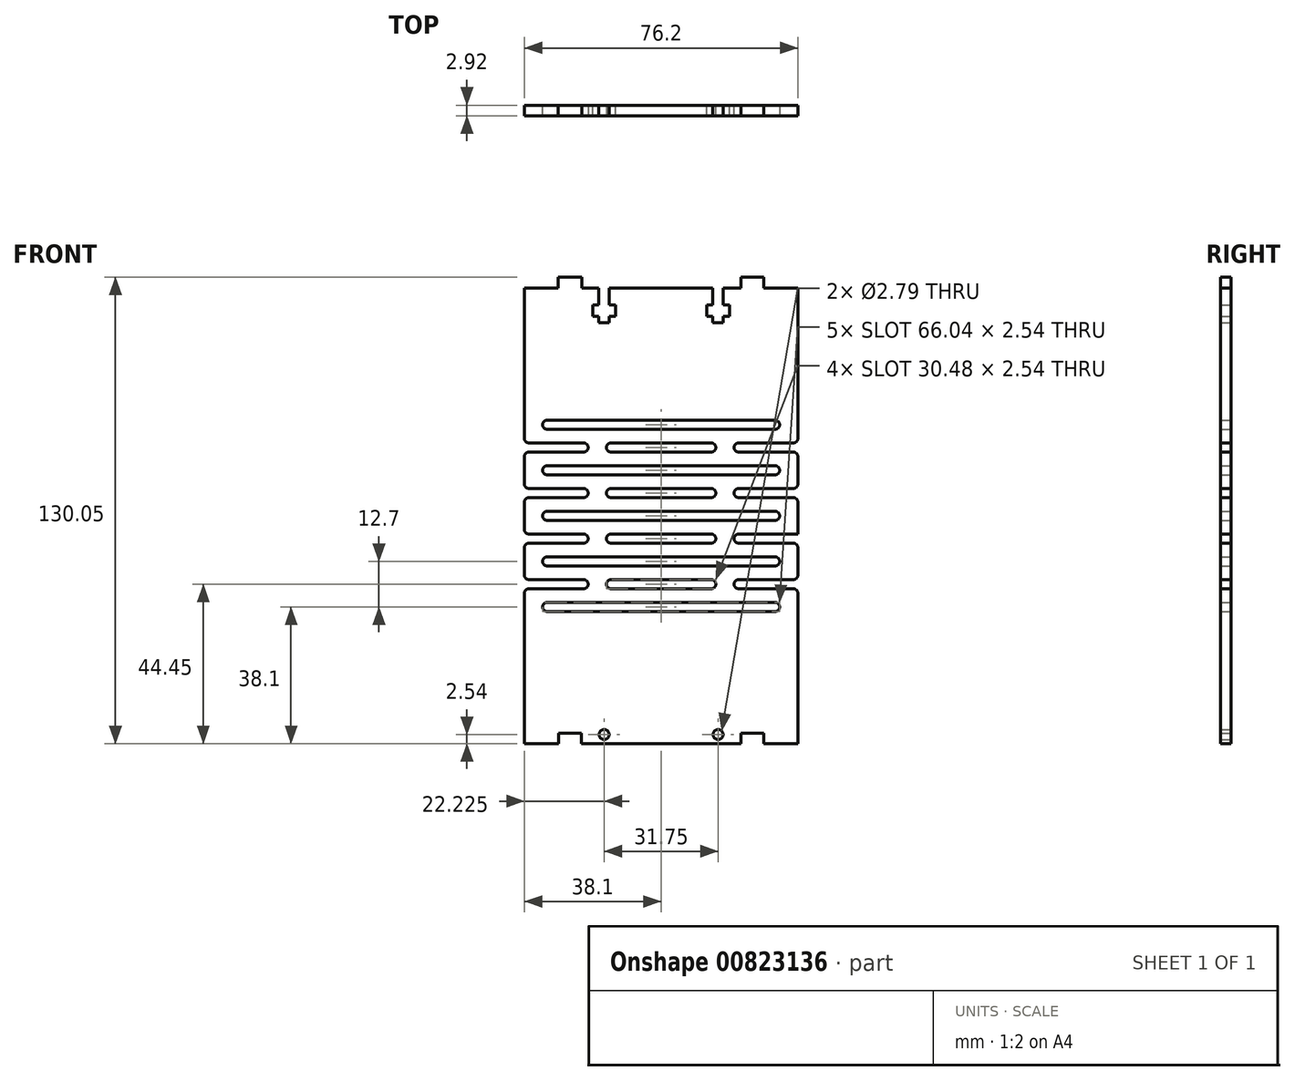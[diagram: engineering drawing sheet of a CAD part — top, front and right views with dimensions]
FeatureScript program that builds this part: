
annotation { "Feature Type Name" : "Feature", "Feature Type Description" : "" }
export const myFeature = defineFeature(function(context is Context, id is Id, definition is map)
    precondition{}
    {
        {
            var Q0;
            Q0=qCreatedBy(makeId("Front.planeOp"),FACE);
            var sketch = newSketch(context, id + "F0", { "sketchPlane" : qUnion([Q0])});
            skLineSegment(sketch, "E0.bottom", {"start": v(0, 0) * mm, "end": v(76.2, 0) * mm});
            skLineSegment(sketch, "E0.top", {"start": v(0, 127) * mm, "end": v(76.2, 127) * mm});
            skLineSegment(sketch, "E0.left", {"start": v(0, 0) * mm, "end": v(0, 127) * mm});
            skLineSegment(sketch, "E0.right", {"start": v(76.2, 0) * mm, "end": v(76.2, 127) * mm});
            skLineSegment(sketch, "E1", {"start": v(0, 0) * mm, "end": v(12.7, 0) * mm});
            skLineSegment(sketch, "E2.bottom", {"start": v(15.88, 2.92) * mm, "end": v(9.53, 2.92) * mm});
            skLineSegment(sketch, "E2.top", {"start": v(15.88, -2.92) * mm, "end": v(9.53, -2.92) * mm});
            skLineSegment(sketch, "E2.left", {"start": v(15.88, 2.92) * mm, "end": v(15.88, -2.92) * mm});
            skLineSegment(sketch, "E2.right", {"start": v(9.53, 2.92) * mm, "end": v(9.53, -2.92) * mm});
            skPoint(sketch, "E2.middle", {"position": v(12.7, 0) * mm});
            skLineSegment(sketch, "E3", {"start": v(76.2, 0) * mm, "end": v(63.5, 0) * mm});
            skLineSegment(sketch, "E4", {"start": v(0, 127) * mm, "end": v(12.7, 127) * mm});
            skLineSegment(sketch, "E5", {"start": v(76.2, 127) * mm, "end": v(63.5, 127) * mm});
            skLineSegment(sketch, "E6.bottom", {"start": v(16, 130.05) * mm, "end": v(9.4, 130.05) * mm});
            skLineSegment(sketch, "E6.top", {"start": v(16, 123.95) * mm, "end": v(9.4, 123.95) * mm});
            skLineSegment(sketch, "E6.left", {"start": v(16, 130.05) * mm, "end": v(16, 123.95) * mm});
            skLineSegment(sketch, "E6.right", {"start": v(9.4, 130.05) * mm, "end": v(9.4, 123.95) * mm});
            skPoint(sketch, "E6.middle", {"position": v(12.7, 127) * mm});
            skLineSegment(sketch, "E7.bottom", {"start": v(60.33, 130.05) * mm, "end": v(66.68, 130.05) * mm});
            skLineSegment(sketch, "E7.top", {"start": v(60.33, 123.95) * mm, "end": v(66.68, 123.95) * mm});
            skLineSegment(sketch, "E7.left", {"start": v(60.32, 130.05) * mm, "end": v(60.32, 123.95) * mm});
            skLineSegment(sketch, "E7.right", {"start": v(66.67, 130.05) * mm, "end": v(66.67, 123.95) * mm});
            skPoint(sketch, "E7.middle", {"position": v(63.5, 127) * mm});
            skLineSegment(sketch, "E8.bottom", {"start": v(60.33, 2.92) * mm, "end": v(66.67, 2.92) * mm});
            skLineSegment(sketch, "E8.top", {"start": v(60.33, -2.92) * mm, "end": v(66.67, -2.92) * mm});
            skLineSegment(sketch, "E8.left", {"start": v(60.33, 2.92) * mm, "end": v(60.33, -2.92) * mm});
            skLineSegment(sketch, "E8.right", {"start": v(66.67, 2.92) * mm, "end": v(66.67, -2.92) * mm});
            skPoint(sketch, "E8.middle", {"position": v(63.5, 0) * mm});
            skCircle(sketch, "E9", {"center": v(53.98, 2.54) * mm, "radius": 1.4 * mm});
            skLineSegment(sketch, "E10", {"start": v(38.1, 0) * mm, "end": v(38.1, 127) * mm});
            skLineSegment(sketch, "E11", {"start": v(60.33, 127) * mm, "end": v(53.98, 127) * mm});
            skLineSegment(sketch, "E12.bottom", {"start": v(55.44, 117.35) * mm, "end": v(52.51, 117.35) * mm});
            skLineSegment(sketch, "E12.top", {"start": v(55.44, 136.65) * mm, "end": v(52.51, 136.65) * mm});
            skLineSegment(sketch, "E12.left", {"start": v(55.44, 117.35) * mm, "end": v(55.44, 136.65) * mm});
            skLineSegment(sketch, "E12.right", {"start": v(52.51, 117.35) * mm, "end": v(52.51, 136.65) * mm});
            skPoint(sketch, "E12.middle", {"position": v(53.98, 127) * mm});
            skLineSegment(sketch, "E13", {"start": v(53.97, 127) * mm, "end": v(53.97, 117.35) * mm});
            skLineSegment(sketch, "E14.bottom", {"start": v(57.15, 122.24) * mm, "end": v(50.8, 122.24) * mm});
            skLineSegment(sketch, "E14.top", {"start": v(57.15, 119.06) * mm, "end": v(50.8, 119.06) * mm});
            skLineSegment(sketch, "E14.left", {"start": v(57.15, 122.24) * mm, "end": v(57.15, 119.06) * mm});
            skLineSegment(sketch, "E14.right", {"start": v(50.8, 122.24) * mm, "end": v(50.8, 119.06) * mm});
            skPoint(sketch, "E14.middle", {"position": v(53.98, 120.65) * mm});
            skCircle(sketch, "E15.MirrorC", {"center": v(22.23, 2.54) * mm, "radius": 1.4 * mm});
            skLineSegment(sketch, "E16.MirrorCS", {"start": v(19.05, 119.06) * mm, "end": v(25.4, 119.06) * mm});
            skLineSegment(sketch, "E17.MirrorCS", {"start": v(22.23, 127) * mm, "end": v(22.23, 117.35) * mm});
            skLineSegment(sketch, "E18.MirrorCS", {"start": v(23.69, 117.35) * mm, "end": v(23.69, 136.65) * mm});
            skPoint(sketch, "E19.MirrorP", {"position": v(22.23, 120.65) * mm});
            skLineSegment(sketch, "E20.MirrorCS", {"start": v(19.05, 122.24) * mm, "end": v(19.05, 119.06) * mm});
            skLineSegment(sketch, "E21.MirrorCS", {"start": v(20.76, 136.65) * mm, "end": v(23.69, 136.65) * mm});
            skPoint(sketch, "E22.MirrorP", {"position": v(22.23, 127) * mm});
            skLineSegment(sketch, "E23.MirrorCS", {"start": v(20.76, 117.35) * mm, "end": v(20.76, 136.65) * mm});
            skLineSegment(sketch, "E24.MirrorCS", {"start": v(25.4, 122.24) * mm, "end": v(25.4, 119.06) * mm});
            skLineSegment(sketch, "E25.MirrorCS", {"start": v(19.05, 122.24) * mm, "end": v(25.4, 122.24) * mm});
            skLineSegment(sketch, "E26.MirrorCS", {"start": v(20.76, 117.35) * mm, "end": v(23.69, 117.35) * mm});
            skLineSegment(sketch, "E27.bottom", {"start": v(71.12, 64.77) * mm, "end": v(5.08, 64.77) * mm});
            skLineSegment(sketch, "E27.top", {"start": v(71.12, 62.23) * mm, "end": v(5.08, 62.23) * mm});
            skLineSegment(sketch, "E27.left", {"start": v(71.12, 64.77) * mm, "end": v(71.12, 62.23) * mm});
            skLineSegment(sketch, "E27.right", {"start": v(5.08, 64.77) * mm, "end": v(5.08, 62.23) * mm});
            skPoint(sketch, "E27.middle", {"position": v(38.1, 63.5) * mm});
            skLineSegment(sketch, "E28.0.1.0", {"start": v(71.12, 77.47) * mm, "end": v(5.08, 77.47) * mm});
            skLineSegment(sketch, "E28.0.1.1", {"start": v(71.12, 74.93) * mm, "end": v(5.08, 74.93) * mm});
            skLineSegment(sketch, "E28.0.1.2", {"start": v(71.12, 77.47) * mm, "end": v(71.12, 74.93) * mm});
            skLineSegment(sketch, "E28.0.1.3", {"start": v(5.08, 77.47) * mm, "end": v(5.08, 74.93) * mm});
            skLineSegment(sketch, "E28.direction1", {"start": v(5.08, 64.77) * mm, "end": v(30.48, 64.77) * mm, "construction": true});
            skLineSegment(sketch, "E28.direction2", {"start": v(5.08, 64.77) * mm, "end": v(5.08, 77.47) * mm, "construction": true});
            skLineSegment(sketch, "E29", {"start": v(38.1, 63.5) * mm, "end": v(38.1, 69.85) * mm});
            skLineSegment(sketch, "E30.bottom", {"start": v(53.34, 68.58) * mm, "end": v(22.86, 68.58) * mm});
            skLineSegment(sketch, "E30.top", {"start": v(53.34, 71.12) * mm, "end": v(22.86, 71.12) * mm});
            skLineSegment(sketch, "E30.left", {"start": v(53.34, 68.58) * mm, "end": v(53.34, 71.12) * mm});
            skLineSegment(sketch, "E30.right", {"start": v(22.86, 68.58) * mm, "end": v(22.86, 71.12) * mm});
            skPoint(sketch, "E30.middle", {"position": v(38.1, 69.85) * mm});
            skLineSegment(sketch, "E31.bottom", {"start": v(58.42, 71.12) * mm, "end": v(93.98, 71.12) * mm});
            skLineSegment(sketch, "E31.top", {"start": v(58.42, 68.58) * mm, "end": v(93.98, 68.58) * mm});
            skLineSegment(sketch, "E31.left", {"start": v(58.42, 71.12) * mm, "end": v(58.42, 68.58) * mm});
            skLineSegment(sketch, "E31.right", {"start": v(93.98, 71.12) * mm, "end": v(93.98, 68.58) * mm});
            skPoint(sketch, "E31.middle", {"position": v(76.2, 69.85) * mm});
            skLineSegment(sketch, "E32.bottom", {"start": v(17.78, 71.12) * mm, "end": v(-17.78, 71.12) * mm});
            skLineSegment(sketch, "E32.top", {"start": v(17.78, 68.58) * mm, "end": v(-17.78, 68.58) * mm});
            skLineSegment(sketch, "E32.left", {"start": v(17.78, 71.12) * mm, "end": v(17.78, 68.58) * mm});
            skLineSegment(sketch, "E32.right", {"start": v(-17.78, 71.12) * mm, "end": v(-17.78, 68.58) * mm});
            skPoint(sketch, "E32.middle", {"position": v(0, 69.85) * mm});
            skPoint(sketch, "E32.cornerSnap0", {"position": v(5.08, 71.12) * mm});
            skLineSegment(sketch, "E33.0.1.0", {"start": v(53.34, 81.28) * mm, "end": v(53.34, 83.82) * mm});
            skLineSegment(sketch, "E33.0.1.1", {"start": v(17.78, 81.28) * mm, "end": v(-17.78, 81.28) * mm});
            skLineSegment(sketch, "E33.0.1.2", {"start": v(53.34, 83.82) * mm, "end": v(22.86, 83.82) * mm});
            skPoint(sketch, "E33.0.1.3", {"position": v(76.2, 82.55) * mm});
            skLineSegment(sketch, "E33.0.1.4", {"start": v(-17.78, 83.82) * mm, "end": v(-17.78, 81.28) * mm});
            skLineSegment(sketch, "E33.0.1.5", {"start": v(58.42, 83.82) * mm, "end": v(93.98, 83.82) * mm});
            skPoint(sketch, "E33.0.1.6", {"position": v(5.08, 83.82) * mm});
            skPoint(sketch, "E33.0.1.7", {"position": v(0, 82.55) * mm});
            skPoint(sketch, "E33.0.1.8", {"position": v(38.1, 82.55) * mm});
            skLineSegment(sketch, "E33.0.1.9", {"start": v(58.42, 81.28) * mm, "end": v(93.98, 81.28) * mm});
            skLineSegment(sketch, "E33.0.1.10", {"start": v(17.78, 83.82) * mm, "end": v(17.78, 81.28) * mm});
            skLineSegment(sketch, "E33.0.1.11", {"start": v(22.86, 81.28) * mm, "end": v(22.86, 83.82) * mm});
            skLineSegment(sketch, "E33.0.1.12", {"start": v(5.08, 77.47) * mm, "end": v(5.08, 90.17) * mm, "construction": true});
            skLineSegment(sketch, "E33.0.1.13", {"start": v(53.34, 81.28) * mm, "end": v(22.86, 81.28) * mm});
            skLineSegment(sketch, "E33.0.1.14", {"start": v(17.78, 83.82) * mm, "end": v(-17.78, 83.82) * mm});
            skLineSegment(sketch, "E33.0.1.15", {"start": v(93.98, 83.82) * mm, "end": v(93.98, 81.28) * mm});
            skLineSegment(sketch, "E33.0.1.16", {"start": v(38.1, 76.2) * mm, "end": v(38.1, 82.55) * mm});
            skLineSegment(sketch, "E33.0.1.17", {"start": v(58.42, 83.82) * mm, "end": v(58.42, 81.28) * mm});
            skLineSegment(sketch, "E33.direction1", {"start": v(-17.78, 68.58) * mm, "end": v(7.62, 68.58) * mm, "construction": true});
            skLineSegment(sketch, "E33.direction2", {"start": v(-17.78, 68.58) * mm, "end": v(-17.78, 81.28) * mm, "construction": true});
            skLineSegment(sketch, "E34", {"start": v(0, 63.5) * mm, "end": v(76.2, 63.5) * mm});
            skLineSegment(sketch, "E35.MirrorCS", {"start": v(38.1, 50.8) * mm, "end": v(38.1, 44.45) * mm});
            skLineSegment(sketch, "E36.MirrorCS", {"start": v(5.08, 49.53) * mm, "end": v(5.08, 52.07) * mm});
            skLineSegment(sketch, "E37.MirrorCS", {"start": v(38.1, 63.5) * mm, "end": v(38.1, 57.15) * mm});
            skLineSegment(sketch, "E38.MirrorCS", {"start": v(-17.78, 55.88) * mm, "end": v(-17.78, 58.42) * mm});
            skLineSegment(sketch, "E39.MirrorCS", {"start": v(53.34, 45.72) * mm, "end": v(53.34, 43.18) * mm});
            skPoint(sketch, "E40.MirrorP", {"position": v(76.2, 44.45) * mm});
            skLineSegment(sketch, "E41.MirrorCS", {"start": v(58.42, 55.88) * mm, "end": v(58.42, 58.42) * mm});
            skLineSegment(sketch, "E42.MirrorCS", {"start": v(76.2, 127) * mm, "end": v(76.2, 0) * mm});
            skLineSegment(sketch, "E43.MirrorCS", {"start": v(0, 127) * mm, "end": v(0, 0) * mm});
            skLineSegment(sketch, "E44.MirrorCS", {"start": v(5.08, 62.23) * mm, "end": v(5.08, 49.53) * mm, "construction": true});
            skLineSegment(sketch, "E45.MirrorCS", {"start": v(53.34, 58.42) * mm, "end": v(22.86, 58.42) * mm});
            skLineSegment(sketch, "E46.MirrorCS", {"start": v(38.1, 127) * mm, "end": v(38.1, 0) * mm});
            skLineSegment(sketch, "E47.MirrorCS", {"start": v(58.42, 43.18) * mm, "end": v(58.42, 45.72) * mm});
            skLineSegment(sketch, "E48.MirrorCS", {"start": v(53.34, 45.72) * mm, "end": v(22.86, 45.72) * mm});
            skLineSegment(sketch, "E49.MirrorCS", {"start": v(53.34, 43.18) * mm, "end": v(22.86, 43.18) * mm});
            skLineSegment(sketch, "E50.MirrorCS", {"start": v(58.42, 58.42) * mm, "end": v(93.98, 58.42) * mm});
            skLineSegment(sketch, "E51.MirrorCS", {"start": v(93.98, 43.18) * mm, "end": v(93.98, 45.72) * mm});
            skLineSegment(sketch, "E52.MirrorCS", {"start": v(93.98, 55.88) * mm, "end": v(93.98, 58.42) * mm});
            skPoint(sketch, "E53.MirrorP", {"position": v(5.08, 55.88) * mm});
            skLineSegment(sketch, "E54.MirrorCS", {"start": v(17.78, 45.72) * mm, "end": v(-17.78, 45.72) * mm});
            skLineSegment(sketch, "E55.MirrorCS", {"start": v(17.78, 43.18) * mm, "end": v(-17.78, 43.18) * mm});
            skPoint(sketch, "E56.MirrorP", {"position": v(5.08, 43.18) * mm});
            skLineSegment(sketch, "E57.MirrorCS", {"start": v(-17.78, 43.18) * mm, "end": v(-17.78, 45.72) * mm});
            skLineSegment(sketch, "E58.MirrorCS", {"start": v(-17.78, 58.42) * mm, "end": v(7.62, 58.42) * mm, "construction": true});
            skLineSegment(sketch, "E59.MirrorCS", {"start": v(58.42, 55.88) * mm, "end": v(93.98, 55.88) * mm});
            skLineSegment(sketch, "E60.MirrorCS", {"start": v(5.08, 49.53) * mm, "end": v(5.08, 36.83) * mm, "construction": true});
            skLineSegment(sketch, "E61.MirrorCS", {"start": v(22.86, 58.42) * mm, "end": v(22.86, 55.88) * mm});
            skPoint(sketch, "E62.MirrorP", {"position": v(0, 57.15) * mm});
            skLineSegment(sketch, "E63.MirrorCS", {"start": v(71.12, 49.53) * mm, "end": v(71.12, 52.07) * mm});
            skLineSegment(sketch, "E64.MirrorCS", {"start": v(71.12, 49.53) * mm, "end": v(5.08, 49.53) * mm});
            skLineSegment(sketch, "E65.MirrorCS", {"start": v(53.34, 58.42) * mm, "end": v(53.34, 55.88) * mm});
            skLineSegment(sketch, "E66.MirrorCS", {"start": v(17.78, 43.18) * mm, "end": v(17.78, 45.72) * mm});
            skLineSegment(sketch, "E67.MirrorCS", {"start": v(71.12, 52.07) * mm, "end": v(5.08, 52.07) * mm});
            skLineSegment(sketch, "E68.MirrorCS", {"start": v(53.34, 55.88) * mm, "end": v(22.86, 55.88) * mm});
            skLineSegment(sketch, "E69.MirrorCS", {"start": v(17.78, 55.88) * mm, "end": v(-17.78, 55.88) * mm});
            skLineSegment(sketch, "E70.MirrorCS", {"start": v(22.86, 45.72) * mm, "end": v(22.86, 43.18) * mm});
            skLineSegment(sketch, "E71.MirrorCS", {"start": v(-17.78, 58.42) * mm, "end": v(-17.78, 45.72) * mm, "construction": true});
            skLineSegment(sketch, "E72.MirrorCS", {"start": v(58.42, 43.18) * mm, "end": v(93.98, 43.18) * mm});
            skLineSegment(sketch, "E73.MirrorCS", {"start": v(17.78, 58.42) * mm, "end": v(-17.78, 58.42) * mm});
            skPoint(sketch, "E74.MirrorP", {"position": v(76.2, 57.15) * mm});
            skPoint(sketch, "E75.MirrorP", {"position": v(38.1, 44.45) * mm});
            skLineSegment(sketch, "E76.MirrorCS", {"start": v(58.42, 45.72) * mm, "end": v(93.98, 45.72) * mm});
            skLineSegment(sketch, "E77.MirrorCS", {"start": v(17.78, 55.88) * mm, "end": v(17.78, 58.42) * mm});
            skPoint(sketch, "E78.MirrorP", {"position": v(38.1, 57.15) * mm});
            skPoint(sketch, "E79.MirrorP", {"position": v(0, 44.45) * mm});
            skLineSegment(sketch, "E80.0.0.2", {"start": v(71.12, 90.17) * mm, "end": v(5.08, 90.17) * mm});
            skLineSegment(sketch, "E80.3.0.2", {"start": v(71.12, 87.63) * mm, "end": v(5.08, 87.63) * mm});
            skLineSegment(sketch, "E80.6.0.2", {"start": v(71.12, 90.17) * mm, "end": v(71.12, 87.63) * mm});
            skLineSegment(sketch, "E80.9.0.2", {"start": v(5.08, 90.17) * mm, "end": v(5.08, 87.63) * mm});
            skLineSegment(sketch, "E81.MirrorCS", {"start": v(71.12, 39.37) * mm, "end": v(5.08, 39.37) * mm});
            skLineSegment(sketch, "E82.MirrorCS", {"start": v(71.12, 36.83) * mm, "end": v(5.08, 36.83) * mm});
            skLineSegment(sketch, "E83.MirrorCS", {"start": v(71.12, 36.83) * mm, "end": v(71.12, 39.37) * mm});
            skLineSegment(sketch, "E84", {"start": v(5.08, 39.37) * mm, "end": v(5.08, 36.83) * mm});
            skSolve(sketch);
        }
        {
            var Q0;
            {var subQ32=sQuery(id+"F0.wireOp",EDGE,"E7.top");Q0=makeQuery(id+"F0.imprint","IMPRINT",FACE,{"disambiguationData":[TD([[makeQuery(id+"F0.imprint","IMPRINT",EDGE,{"derivedFrom":subQ32}),-1.0]])]});}
            var Q1;
            {var subQ25=sQuery(id+"F0.wireOp",EDGE,"E6.top");Q1=makeQuery(id+"F0.imprint","IMPRINT",FACE,{"disambiguationData":[TD([[makeQuery(id+"F0.imprint","IMPRINT",EDGE,{"derivedFrom":subQ25}),1.0]])]});}
            var Q2;
            {var subQ29=sQuery(id+"F0.wireOp",EDGE,"E8.bottom");Q2=makeQuery(id+"F0.imprint","IMPRINT",FACE,{"disambiguationData":[TD([[makeQuery(id+"F0.imprint","IMPRINT",EDGE,{"derivedFrom":subQ29}),1.0]])]});}
            var Q3;
            {var subQ25=sQuery(id+"F0.wireOp",EDGE,"E2.bottom");Q3=makeQuery(id+"F0.imprint","IMPRINT",FACE,{"disambiguationData":[TD([[makeQuery(id+"F0.imprint","IMPRINT",EDGE,{"derivedFrom":subQ25}),-1.0]])]});}
            var Q4;
            {var subQ0=sQuery(id+"F0.wireOp",EDGE,"E7.top");Q4=makeQuery(id+"F0.imprint","IMPRINT",FACE,{"disambiguationData":[TD([[makeQuery(id+"F0.imprint","IMPRINT",EDGE,{"derivedFrom":subQ0}),1.0]])]});}
            var Q5;
            {var subQ1=sQuery(id+"F0.wireOp",EDGE,"E7.bottom");Q5=makeQuery(id+"F0.imprint","IMPRINT",FACE,{"disambiguationData":[TD([[makeQuery(id+"F0.imprint","IMPRINT",EDGE,{"derivedFrom":subQ1}),-1.0]])]});}
            var Q6;
            {var subQ0=sQuery(id+"F0.wireOp",EDGE,"E6.top");Q6=makeQuery(id+"F0.imprint","IMPRINT",FACE,{"disambiguationData":[TD([[makeQuery(id+"F0.imprint","IMPRINT",EDGE,{"derivedFrom":subQ0}),-1.0]])]});}
            var Q7;
            {var subQ0=sQuery(id+"F0.wireOp",EDGE,"E6.bottom");Q7=makeQuery(id+"F0.imprint","IMPRINT",FACE,{"disambiguationData":[TD([[makeQuery(id+"F0.imprint","IMPRINT",EDGE,{"derivedFrom":subQ0}),1.0]])]});}
            extrude(context, id + "F1", {"entities" : qUnion([Q0, Q1, Q2, Q3, Q4, Q5, Q6, Q7]), "depth" : 2.92 * mm, "offsetDistance" : 25.4 * mm});
        }
        {
            var Q0;
            Q0=makeQuery(id+"F1.opExtrude","SWEPT_EDGE",EDGE,{"disambiguationData":[OSD([sQuery(id+"F0.wireOp",EDGE,"E42.MirrorCS"),sQuery(id+"F0.wireOp",EDGE,"E72.MirrorCS")])]});
            var Q1;
            Q1=makeQuery(id+"F1.opExtrude","SWEPT_EDGE",EDGE,{"disambiguationData":[OSD([sQuery(id+"F0.wireOp",EDGE,"E42.MirrorCS"),sQuery(id+"F0.wireOp",EDGE,"E76.MirrorCS")])]});
            var Q2;
            Q2=makeQuery(id+"F1.opExtrude","SWEPT_EDGE",EDGE,{"disambiguationData":[OSD([sQuery(id+"F0.wireOp",EDGE,"E42.MirrorCS"),sQuery(id+"F0.wireOp",EDGE,"E59.MirrorCS")])]});
            var Q3;
            Q3=makeQuery(id+"F1.opExtrude","SWEPT_EDGE",EDGE,{"disambiguationData":[OSD([sQuery(id+"F0.wireOp",EDGE,"E31.top"),sQuery(id+"F0.wireOp",EDGE,"E42.MirrorCS")])]});
            var Q4;
            Q4=makeQuery(id+"F1.opExtrude","SWEPT_EDGE",EDGE,{"disambiguationData":[OSD([sQuery(id+"F0.wireOp",EDGE,"E31.bottom"),sQuery(id+"F0.wireOp",EDGE,"E42.MirrorCS")])]});
            var Q5;
            Q5=makeQuery(id+"F1.opExtrude","SWEPT_EDGE",EDGE,{"disambiguationData":[OSD([sQuery(id+"F0.wireOp",EDGE,"E33.0.1.9"),sQuery(id+"F0.wireOp",EDGE,"E42.MirrorCS")])]});
            var Q6;
            Q6=makeQuery(id+"F1.opExtrude","SWEPT_EDGE",EDGE,{"disambiguationData":[OSD([sQuery(id+"F0.wireOp",EDGE,"E33.0.1.5"),sQuery(id+"F0.wireOp",EDGE,"E42.MirrorCS")])]});
            var Q7;
            Q7=makeQuery(id+"F1.opExtrude","SWEPT_EDGE",EDGE,{"disambiguationData":[OSD([sQuery(id+"F0.wireOp",EDGE,"E33.0.1.9"),sQuery(id+"F0.wireOp",EDGE,"E33.0.1.17")])]});
            var Q8;
            Q8=makeQuery(id+"F1.opExtrude","SWEPT_EDGE",EDGE,{"disambiguationData":[OSD([sQuery(id+"F0.wireOp",EDGE,"E31.top"),sQuery(id+"F0.wireOp",EDGE,"E31.left")])]});
            var Q9;
            Q9=makeQuery(id+"F1.opExtrude","SWEPT_EDGE",EDGE,{"disambiguationData":[OSD([sQuery(id+"F0.wireOp",EDGE,"E41.MirrorCS"),sQuery(id+"F0.wireOp",EDGE,"E59.MirrorCS")])]});
            var Q10;
            Q10=makeQuery(id+"F1.opExtrude","SWEPT_EDGE",EDGE,{"disambiguationData":[OSD([sQuery(id+"F0.wireOp",EDGE,"E47.MirrorCS"),sQuery(id+"F0.wireOp",EDGE,"E72.MirrorCS")])]});
            var Q11;
            Q11=makeQuery(id+"F1.opExtrude","SWEPT_EDGE",EDGE,{"disambiguationData":[OSD([sQuery(id+"F0.wireOp",EDGE,"E49.MirrorCS"),sQuery(id+"F0.wireOp",EDGE,"E70.MirrorCS")])]});
            var Q12;
            Q12=makeQuery(id+"F1.opExtrude","SWEPT_EDGE",EDGE,{"disambiguationData":[OSD([sQuery(id+"F0.wireOp",EDGE,"E33.0.1.11"),sQuery(id+"F0.wireOp",EDGE,"E33.0.1.13")])]});
            var Q13;
            Q13=makeQuery(id+"F1.opExtrude","SWEPT_EDGE",EDGE,{"disambiguationData":[OSD([sQuery(id+"F0.wireOp",EDGE,"E30.bottom"),sQuery(id+"F0.wireOp",EDGE,"E30.right")])]});
            var Q14;
            Q14=makeQuery(id+"F1.opExtrude","SWEPT_EDGE",EDGE,{"disambiguationData":[OSD([sQuery(id+"F0.wireOp",EDGE,"E61.MirrorCS"),sQuery(id+"F0.wireOp",EDGE,"E68.MirrorCS")])]});
            var Q15;
            Q15=makeQuery(id+"F1.opExtrude","SWEPT_EDGE",EDGE,{"disambiguationData":[OSD([sQuery(id+"F0.wireOp",EDGE,"E82.MirrorCS"),sQuery(id+"F0.wireOp",EDGE,"E84")])]});
            var Q16;
            Q16=makeQuery(id+"F1.opExtrude","SWEPT_EDGE",EDGE,{"disambiguationData":[OSD([sQuery(id+"F0.wireOp",EDGE,"E36.MirrorCS"),sQuery(id+"F0.wireOp",EDGE,"E64.MirrorCS")])]});
            var Q17;
            Q17=makeQuery(id+"F1.opExtrude","SWEPT_EDGE",EDGE,{"disambiguationData":[OSD([sQuery(id+"F0.wireOp",EDGE,"E27.top"),sQuery(id+"F0.wireOp",EDGE,"E27.right")])]});
            var Q18;
            Q18=makeQuery(id+"F1.opExtrude","SWEPT_EDGE",EDGE,{"disambiguationData":[OSD([sQuery(id+"F0.wireOp",EDGE,"E28.0.1.1"),sQuery(id+"F0.wireOp",EDGE,"E28.0.1.3")])]});
            var Q19;
            Q19=makeQuery(id+"F1.opExtrude","SWEPT_EDGE",EDGE,{"disambiguationData":[OSD([sQuery(id+"F0.wireOp",EDGE,"E80.3.0.2"),sQuery(id+"F0.wireOp",EDGE,"E80.9.0.2")])]});
            var Q20;
            Q20=makeQuery(id+"F1.opExtrude","SWEPT_EDGE",EDGE,{"disambiguationData":[OSD([sQuery(id+"F0.wireOp",EDGE,"E80.3.0.2"),sQuery(id+"F0.wireOp",EDGE,"E80.6.0.2")])]});
            var Q21;
            Q21=makeQuery(id+"F1.opExtrude","SWEPT_EDGE",EDGE,{"disambiguationData":[OSD([sQuery(id+"F0.wireOp",EDGE,"E28.0.1.1"),sQuery(id+"F0.wireOp",EDGE,"E28.0.1.2")])]});
            var Q22;
            Q22=makeQuery(id+"F1.opExtrude","SWEPT_EDGE",EDGE,{"disambiguationData":[OSD([sQuery(id+"F0.wireOp",EDGE,"E27.top"),sQuery(id+"F0.wireOp",EDGE,"E27.left")])]});
            var Q23;
            Q23=makeQuery(id+"F1.opExtrude","SWEPT_EDGE",EDGE,{"disambiguationData":[OSD([sQuery(id+"F0.wireOp",EDGE,"E63.MirrorCS"),sQuery(id+"F0.wireOp",EDGE,"E64.MirrorCS")])]});
            var Q24;
            Q24=makeQuery(id+"F1.opExtrude","SWEPT_EDGE",EDGE,{"disambiguationData":[OSD([sQuery(id+"F0.wireOp",EDGE,"E82.MirrorCS"),sQuery(id+"F0.wireOp",EDGE,"E83.MirrorCS")])]});
            var Q25;
            Q25=makeQuery(id+"F1.opExtrude","SWEPT_EDGE",EDGE,{"disambiguationData":[OSD([sQuery(id+"F0.wireOp",EDGE,"E43.MirrorCS"),sQuery(id+"F0.wireOp",EDGE,"E55.MirrorCS")])]});
            var Q26;
            Q26=makeQuery(id+"F1.opExtrude","SWEPT_EDGE",EDGE,{"disambiguationData":[OSD([sQuery(id+"F0.wireOp",EDGE,"E43.MirrorCS"),sQuery(id+"F0.wireOp",EDGE,"E54.MirrorCS")])]});
            var Q27;
            Q27=makeQuery(id+"F1.opExtrude","SWEPT_EDGE",EDGE,{"disambiguationData":[OSD([sQuery(id+"F0.wireOp",EDGE,"E43.MirrorCS"),sQuery(id+"F0.wireOp",EDGE,"E69.MirrorCS")])]});
            var Q28;
            Q28=makeQuery(id+"F1.opExtrude","SWEPT_EDGE",EDGE,{"disambiguationData":[OSD([sQuery(id+"F0.wireOp",EDGE,"E43.MirrorCS"),sQuery(id+"F0.wireOp",EDGE,"E73.MirrorCS")])]});
            var Q29;
            Q29=makeQuery(id+"F1.opExtrude","SWEPT_EDGE",EDGE,{"disambiguationData":[OSD([sQuery(id+"F0.wireOp",EDGE,"E32.top"),sQuery(id+"F0.wireOp",EDGE,"E43.MirrorCS")])]});
            var Q30;
            Q30=makeQuery(id+"F1.opExtrude","SWEPT_EDGE",EDGE,{"disambiguationData":[OSD([sQuery(id+"F0.wireOp",EDGE,"E32.bottom"),sQuery(id+"F0.wireOp",EDGE,"E43.MirrorCS")])]});
            var Q31;
            Q31=makeQuery(id+"F1.opExtrude","SWEPT_EDGE",EDGE,{"disambiguationData":[OSD([sQuery(id+"F0.wireOp",EDGE,"E33.0.1.1"),sQuery(id+"F0.wireOp",EDGE,"E43.MirrorCS")])]});
            var Q32;
            Q32=makeQuery(id+"F1.opExtrude","SWEPT_EDGE",EDGE,{"disambiguationData":[OSD([sQuery(id+"F0.wireOp",EDGE,"E33.0.1.14"),sQuery(id+"F0.wireOp",EDGE,"E43.MirrorCS")])]});
            var Q33;
            Q33=makeQuery(id+"F1.opExtrude","SWEPT_EDGE",EDGE,{"disambiguationData":[OSD([sQuery(id+"F0.wireOp",EDGE,"E39.MirrorCS"),sQuery(id+"F0.wireOp",EDGE,"E49.MirrorCS")])]});
            var Q34;
            Q34=makeQuery(id+"F1.opExtrude","SWEPT_EDGE",EDGE,{"disambiguationData":[OSD([sQuery(id+"F0.wireOp",EDGE,"E65.MirrorCS"),sQuery(id+"F0.wireOp",EDGE,"E68.MirrorCS")])]});
            var Q35;
            Q35=makeQuery(id+"F1.opExtrude","SWEPT_EDGE",EDGE,{"disambiguationData":[OSD([sQuery(id+"F0.wireOp",EDGE,"E30.bottom"),sQuery(id+"F0.wireOp",EDGE,"E30.left")])]});
            var Q36;
            Q36=makeQuery(id+"F1.opExtrude","SWEPT_EDGE",EDGE,{"disambiguationData":[OSD([sQuery(id+"F0.wireOp",EDGE,"E33.0.1.0"),sQuery(id+"F0.wireOp",EDGE,"E33.0.1.13")])]});
            var Q37;
            Q37=makeQuery(id+"F1.opExtrude","SWEPT_EDGE",EDGE,{"disambiguationData":[OSD([sQuery(id+"F0.wireOp",EDGE,"E81.MirrorCS"),sQuery(id+"F0.wireOp",EDGE,"E83.MirrorCS")])]});
            var Q38;
            Q38=makeQuery(id+"F1.opExtrude","SWEPT_EDGE",EDGE,{"disambiguationData":[OSD([sQuery(id+"F0.wireOp",EDGE,"E27.bottom"),sQuery(id+"F0.wireOp",EDGE,"E27.left")])]});
            var Q39;
            Q39=makeQuery(id+"F1.opExtrude","SWEPT_EDGE",EDGE,{"disambiguationData":[OSD([sQuery(id+"F0.wireOp",EDGE,"E63.MirrorCS"),sQuery(id+"F0.wireOp",EDGE,"E67.MirrorCS")])]});
            var Q40;
            Q40=makeQuery(id+"F1.opExtrude","SWEPT_EDGE",EDGE,{"disambiguationData":[OSD([sQuery(id+"F0.wireOp",EDGE,"E28.0.1.0"),sQuery(id+"F0.wireOp",EDGE,"E28.0.1.2")])]});
            var Q41;
            Q41=makeQuery(id+"F1.opExtrude","SWEPT_EDGE",EDGE,{"disambiguationData":[OSD([sQuery(id+"F0.wireOp",EDGE,"E80.0.0.2"),sQuery(id+"F0.wireOp",EDGE,"E80.6.0.2")])]});
            var Q42;
            Q42=makeQuery(id+"F1.opExtrude","SWEPT_EDGE",EDGE,{"disambiguationData":[OSD([sQuery(id+"F0.wireOp",EDGE,"E33.0.1.0"),sQuery(id+"F0.wireOp",EDGE,"E33.0.1.2")])]});
            var Q43;
            Q43=makeQuery(id+"F1.opExtrude","SWEPT_EDGE",EDGE,{"disambiguationData":[OSD([sQuery(id+"F0.wireOp",EDGE,"E45.MirrorCS"),sQuery(id+"F0.wireOp",EDGE,"E65.MirrorCS")])]});
            var Q44;
            Q44=makeQuery(id+"F1.opExtrude","SWEPT_EDGE",EDGE,{"disambiguationData":[OSD([sQuery(id+"F0.wireOp",EDGE,"E39.MirrorCS"),sQuery(id+"F0.wireOp",EDGE,"E48.MirrorCS")])]});
            var Q45;
            Q45=makeQuery(id+"F1.opExtrude","SWEPT_EDGE",EDGE,{"disambiguationData":[OSD([sQuery(id+"F0.wireOp",EDGE,"E54.MirrorCS"),sQuery(id+"F0.wireOp",EDGE,"E66.MirrorCS")])]});
            var Q46;
            Q46=makeQuery(id+"F1.opExtrude","SWEPT_EDGE",EDGE,{"disambiguationData":[OSD([sQuery(id+"F0.wireOp",EDGE,"E73.MirrorCS"),sQuery(id+"F0.wireOp",EDGE,"E77.MirrorCS")])]});
            var Q47;
            Q47=makeQuery(id+"F1.opExtrude","SWEPT_EDGE",EDGE,{"disambiguationData":[OSD([sQuery(id+"F0.wireOp",EDGE,"E32.bottom"),sQuery(id+"F0.wireOp",EDGE,"E32.left")])]});
            var Q48;
            Q48=makeQuery(id+"F1.opExtrude","SWEPT_EDGE",EDGE,{"disambiguationData":[OSD([sQuery(id+"F0.wireOp",EDGE,"E33.0.1.10"),sQuery(id+"F0.wireOp",EDGE,"E33.0.1.14")])]});
            var Q49;
            Q49=makeQuery(id+"F1.opExtrude","SWEPT_EDGE",EDGE,{"disambiguationData":[OSD([sQuery(id+"F0.wireOp",EDGE,"E81.MirrorCS"),sQuery(id+"F0.wireOp",EDGE,"E84")])]});
            var Q50;
            Q50=makeQuery(id+"F1.opExtrude","SWEPT_EDGE",EDGE,{"disambiguationData":[OSD([sQuery(id+"F0.wireOp",EDGE,"E36.MirrorCS"),sQuery(id+"F0.wireOp",EDGE,"E67.MirrorCS")])]});
            var Q51;
            Q51=makeQuery(id+"F1.opExtrude","SWEPT_EDGE",EDGE,{"disambiguationData":[OSD([sQuery(id+"F0.wireOp",EDGE,"E27.bottom"),sQuery(id+"F0.wireOp",EDGE,"E27.right")])]});
            var Q52;
            Q52=makeQuery(id+"F1.opExtrude","SWEPT_EDGE",EDGE,{"disambiguationData":[OSD([sQuery(id+"F0.wireOp",EDGE,"E28.0.1.0"),sQuery(id+"F0.wireOp",EDGE,"E28.0.1.3")])]});
            var Q53;
            Q53=makeQuery(id+"F1.opExtrude","SWEPT_EDGE",EDGE,{"disambiguationData":[OSD([sQuery(id+"F0.wireOp",EDGE,"E80.0.0.2"),sQuery(id+"F0.wireOp",EDGE,"E80.9.0.2")])]});
            var Q54;
            Q54=makeQuery(id+"F1.opExtrude","SWEPT_EDGE",EDGE,{"disambiguationData":[OSD([sQuery(id+"F0.wireOp",EDGE,"E48.MirrorCS"),sQuery(id+"F0.wireOp",EDGE,"E70.MirrorCS")])]});
            var Q55;
            Q55=makeQuery(id+"F1.opExtrude","SWEPT_EDGE",EDGE,{"disambiguationData":[OSD([sQuery(id+"F0.wireOp",EDGE,"E45.MirrorCS"),sQuery(id+"F0.wireOp",EDGE,"E61.MirrorCS")])]});
            var Q56;
            Q56=makeQuery(id+"F1.opExtrude","SWEPT_EDGE",EDGE,{"disambiguationData":[OSD([sQuery(id+"F0.wireOp",EDGE,"E33.0.1.2"),sQuery(id+"F0.wireOp",EDGE,"E33.0.1.11")])]});
            var Q57;
            Q57=makeQuery(id+"F1.opExtrude","SWEPT_EDGE",EDGE,{"disambiguationData":[OSD([sQuery(id+"F0.wireOp",EDGE,"E30.top"),sQuery(id+"F0.wireOp",EDGE,"E30.right")])]});
            var Q58;
            Q58=makeQuery(id+"F1.opExtrude","SWEPT_EDGE",EDGE,{"disambiguationData":[OSD([sQuery(id+"F0.wireOp",EDGE,"E30.top"),sQuery(id+"F0.wireOp",EDGE,"E30.left")])]});
            var Q59;
            Q59=makeQuery(id+"F1.opExtrude","SWEPT_EDGE",EDGE,{"disambiguationData":[OSD([sQuery(id+"F0.wireOp",EDGE,"E55.MirrorCS"),sQuery(id+"F0.wireOp",EDGE,"E66.MirrorCS")])]});
            var Q60;
            Q60=makeQuery(id+"F1.opExtrude","SWEPT_EDGE",EDGE,{"disambiguationData":[OSD([sQuery(id+"F0.wireOp",EDGE,"E69.MirrorCS"),sQuery(id+"F0.wireOp",EDGE,"E77.MirrorCS")])]});
            var Q61;
            Q61=makeQuery(id+"F1.opExtrude","SWEPT_EDGE",EDGE,{"disambiguationData":[OSD([sQuery(id+"F0.wireOp",EDGE,"E32.top"),sQuery(id+"F0.wireOp",EDGE,"E32.left")])]});
            var Q62;
            Q62=makeQuery(id+"F1.opExtrude","SWEPT_EDGE",EDGE,{"disambiguationData":[OSD([sQuery(id+"F0.wireOp",EDGE,"E33.0.1.1"),sQuery(id+"F0.wireOp",EDGE,"E33.0.1.10")])]});
            var Q63;
            Q63=makeQuery(id+"F1.opExtrude","SWEPT_EDGE",EDGE,{"disambiguationData":[OSD([sQuery(id+"F0.wireOp",EDGE,"E47.MirrorCS"),sQuery(id+"F0.wireOp",EDGE,"E76.MirrorCS")])]});
            var Q64;
            Q64=makeQuery(id+"F1.opExtrude","SWEPT_EDGE",EDGE,{"disambiguationData":[OSD([sQuery(id+"F0.wireOp",EDGE,"E41.MirrorCS"),sQuery(id+"F0.wireOp",EDGE,"E50.MirrorCS")])]});
            var Q65;
            Q65=makeQuery(id+"F1.opExtrude","SWEPT_EDGE",EDGE,{"disambiguationData":[OSD([sQuery(id+"F0.wireOp",EDGE,"E31.bottom"),sQuery(id+"F0.wireOp",EDGE,"E31.left")])]});
            var Q66;
            Q66=makeQuery(id+"F1.opExtrude","SWEPT_EDGE",EDGE,{"disambiguationData":[OSD([sQuery(id+"F0.wireOp",EDGE,"E33.0.1.5"),sQuery(id+"F0.wireOp",EDGE,"E33.0.1.17")])]});
            fillet(context, id + "F2", {"entities" : qUnion([Q0, Q1, Q2, Q3, Q4, Q5, Q6, Q7, Q8, Q9, Q10, Q11, Q12, Q13, Q14, Q15, Q16, Q17, Q18, Q19, Q20, Q21, Q22, Q23, Q24, Q25, Q26, Q27, Q28, Q29, Q30, Q31, Q32, Q33, Q34, Q35, Q36, Q37, Q38, Q39, Q40, Q41, Q42, Q43, Q44, Q45, Q46, Q47, Q48, Q49, Q50, Q51, Q52, Q53, Q54, Q55, Q56, Q57, Q58, Q59, Q60, Q61, Q62, Q63, Q64, Q65, Q66]), "radius" : 1.27 * mm, "tangentPropagation" : true, "allowEdgeOverflow" : false});
        }
    });
